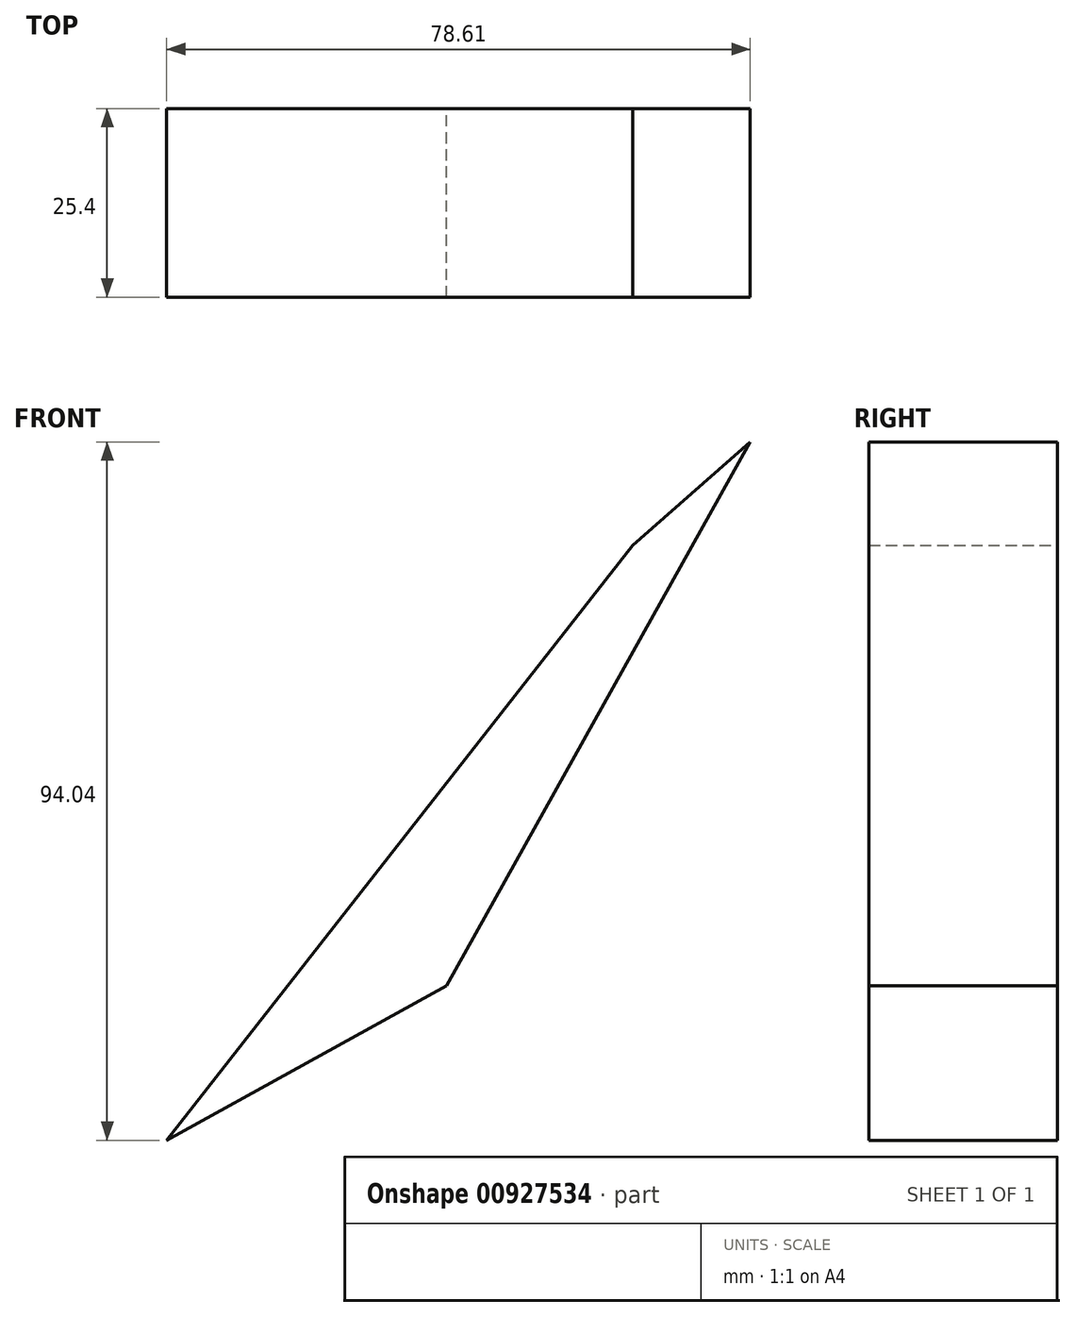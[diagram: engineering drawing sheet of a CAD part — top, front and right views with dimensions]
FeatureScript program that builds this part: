
annotation { "Feature Type Name" : "Feature", "Feature Type Description" : "" }
export const myFeature = defineFeature(function(context is Context, id is Id, definition is map)
    precondition{}
    {
        {
            var Q0;
            Q0=qCreatedBy(makeId("Front.planeOp"),FACE);
            var sketch = newSketch(context, id + "F0", { "sketchPlane" : qUnion([Q0])});
            skLineSegment(sketch, "E0", {"start": v(-52.4, 53.7) * mm, "end": v(62.8, 27.28) * mm});
            skLineSegment(sketch, "E1", {"start": v(62.8, 27.28) * mm, "end": v(-45.47, -68) * mm});
            skLineSegment(sketch, "E2", {"start": v(-45.47, -68) * mm, "end": v(-52.4, 53.7) * mm});
            skLineSegment(sketch, "E3", {"start": v(62.8, 0) * mm, "end": v(78.61, 13.92) * mm});
            skLineSegment(sketch, "E4", {"start": v(78.61, 13.92) * mm, "end": v(37.68, -59.33) * mm});
            skLineSegment(sketch, "E5", {"start": v(37.68, -59.33) * mm, "end": v(0, -80.12) * mm});
            skLineSegment(sketch, "E6", {"start": v(0, -80.12) * mm, "end": v(62.8, 0) * mm});
            skSolve(sketch);
        }
        {
            var Q0;
            Q0=makeQuery(id+"F0.imprint","IMPRINT",FACE,{"disambiguationData":[TD([[makeQuery(id+"F0.imprint","IMPRINT",EDGE,{"derivedFrom":sQuery(id+"F0.wireOp",EDGE,"E3")}),-1.0]])]});
            extrude(context, id + "F1", {"entities" : qUnion([Q0]), "depth" : 25.4 * mm, "offsetDistance" : 25.4 * mm});
        }
    });
